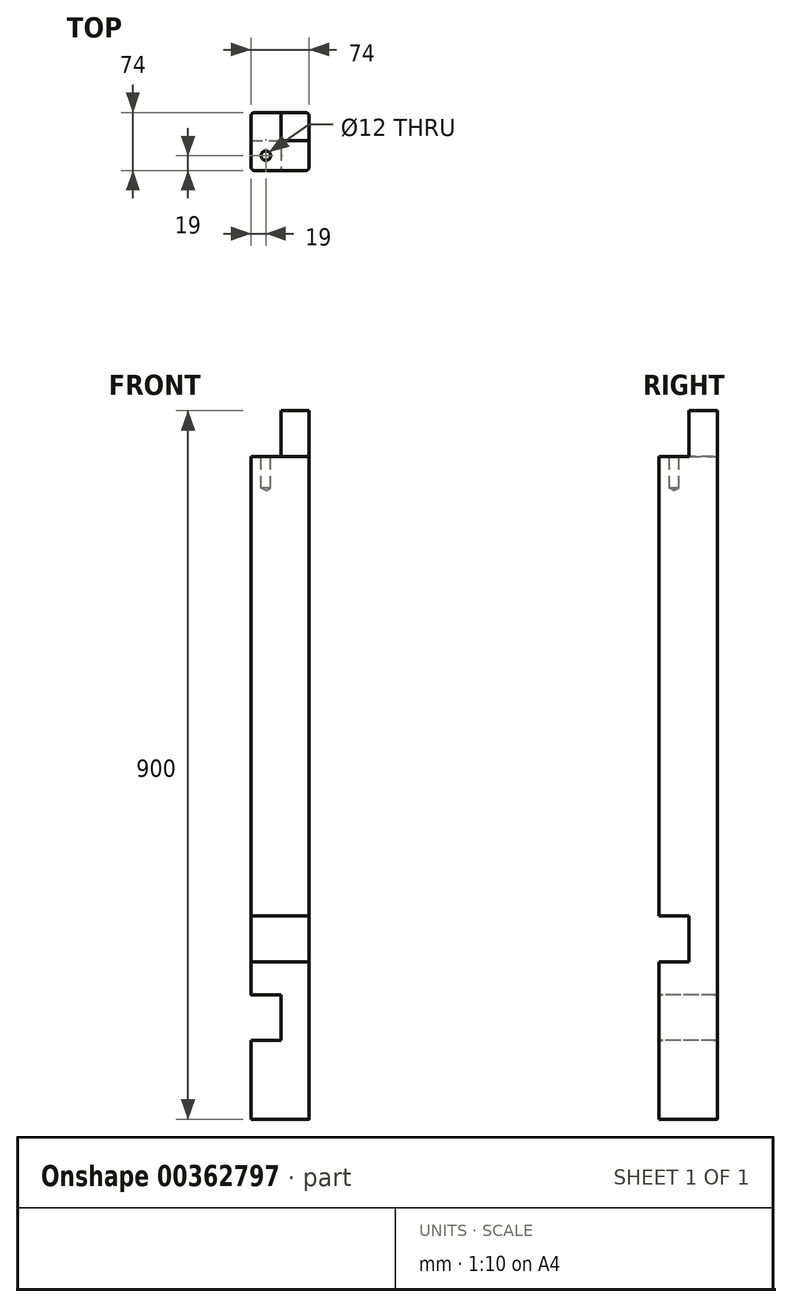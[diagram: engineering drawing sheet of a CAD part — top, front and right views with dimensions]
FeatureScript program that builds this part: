
annotation { "Feature Type Name" : "Feature", "Feature Type Description" : "" }
export const myFeature = defineFeature(function(context is Context, id is Id, definition is map)
    precondition{}
    {
        {
            var Q0;
            Q0=qCreatedBy(makeId("Top.planeOp"),FACE);
            var sketch = newSketch(context, id + "F0", { "sketchPlane" : qUnion([Q0])});
            skLineSegment(sketch, "E0.bottom", {"start": v(37, 37) * mm, "end": v(-37, 37) * mm});
            skLineSegment(sketch, "E0.top", {"start": v(37, -37) * mm, "end": v(-37, -37) * mm});
            skLineSegment(sketch, "E0.left", {"start": v(37, 37) * mm, "end": v(37, -37) * mm});
            skLineSegment(sketch, "E0.right", {"start": v(-37, 37) * mm, "end": v(-37, -37) * mm});
            skPoint(sketch, "E0.middle", {"position": v(0, 0) * mm});
            skSolve(sketch);
        }
        {
            var Q0;
            Q0=makeQuery(id+"F0.imprint","IMPRINT",FACE,{"disambiguationData":[TD([[makeQuery(id+"F0.imprint","IMPRINT",EDGE,{"derivedFrom":sQuery(id+"F0.wireOp",EDGE,"E0.bottom")}),1.0]])]});
            extrude(context, id + "F1", {"entities" : qUnion([Q0]), "oppositeDirection" : true, "depth" : 900 * mm});
        }
        {
            var Q0;
            Q0=makeQuery(id+"F1.opExtrude","SWEPT_FACE",FACE,{"disambiguationData":[OSD([sQuery(id+"F0.wireOp",EDGE,"E0.top")])]});
            var sketch = newSketch(context, id + "F2", { "sketchPlane" : qUnion([Q0])});
            skLineSegment(sketch, "E1", {"start": v(-37, -58) * mm, "end": v(37, -58) * mm});
            skSolve(sketch);
        }
        {
            var Q0;
            Q0=makeQuery(id+"F1.opExtrude","SWEPT_FACE",FACE,{"disambiguationData":[OSD([sQuery(id+"F0.wireOp",EDGE,"E0.right")])]});
            var sketch = newSketch(context, id + "F3", { "sketchPlane" : qUnion([Q0])});
            skLineSegment(sketch, "E2", {"start": v(37, -58) * mm, "end": v(-37, -58) * mm});
            skSolve(sketch);
        }
        {
            var Q0;
            {var subQ0=sQuery(id+"F2.wireOp",EDGE,"E1");Q0=makeQuery(id+"F2.imprint","IMPRINT",FACE,{"disambiguationData":[TD([[makeQuery(id+"F2.imprint","IMPRINT",EDGE,{"derivedFrom":subQ0}),1.0]])]});}
            extrude(context, id + "F4", {"entities" : qUnion([Q0]), "operationType" : NewBodyOperationType.REMOVE, "oppositeDirection" : true, "depth" : 38 * mm});
        }
        {
            var Q0;
            {var subQ0=sQuery(id+"F3.wireOp",EDGE,"E2");Q0=makeQuery(id+"F3.imprint","IMPRINT",FACE,{"disambiguationData":[TD([[makeQuery(id+"F3.imprint","IMPRINT",EDGE,{"derivedFrom":subQ0}),-1.0]])]});}
            extrude(context, id + "F5", {"entities" : qUnion([Q0]), "operationType" : NewBodyOperationType.REMOVE, "oppositeDirection" : true, "depth" : 38 * mm});
        }
        {
            var Q0;
            Q0=makeQuery(id+"F5.boolean.opBoolean","MERGE",FACE,{"derivedFrom":[makeQuery(id+"F4.boolean.opBoolean","COPY",FACE,{"derivedFrom":makeQuery(id+"F4.opExtrude","SWEPT_FACE",FACE,{"disambiguationData":[OSD([sQuery(id+"F2.wireOp",EDGE,"E1")])]})}),makeQuery(id+"F5.opExtrude","SWEPT_FACE",FACE,{"disambiguationData":[OSD([sQuery(id+"F3.wireOp",EDGE,"E2")])]})]});
            var sketch = newSketch(context, id + "F6", { "sketchPlane" : qUnion([Q0])});
            skPoint(sketch, "E3", {"position": v(-18, -18) * mm});
            skSolve(sketch);
        }
        {
            var Q0;
            Q0=sQuery(id+"F6.wireOp",VERTEX,"E3");
            var Q1;
            Q1=makeQuery(id+"F1.opExtrude","SWEPT_BODY",BODY,{"disambiguationData":[OSD([sQuery(id+"F0.wireOp",EDGE,"E0.bottom"),sQuery(id+"F0.wireOp",EDGE,"E0.top"),sQuery(id+"F0.wireOp",EDGE,"E0.left"),sQuery(id+"F0.wireOp",EDGE,"E0.right")])]});
            hole(context, id + "F7", {"style" : HoleStyle.SIMPLE, "endStyle" : HoleEndStyle.BLIND, "holeDiameter" : 12 * mm, "holeDepth" : 40 * mm, "isTappedThrough" : true, "tappedDepth" : 12 * mm, "tapClearance" : 3, "locations" : qUnion([Q0]), "scope" : qUnion([Q1])});
        }
        {
            var Q0;
            Q0=makeQuery(id+"F1.opExtrude","SWEPT_FACE",FACE,{"disambiguationData":[OSD([sQuery(id+"F0.wireOp",EDGE,"E0.right")])]});
            var sketch = newSketch(context, id + "F8", { "sketchPlane" : qUnion([Q0])});
            skLineSegment(sketch, "E4", {"start": v(-37, -742) * mm, "end": v(37, -742) * mm});
            skLineSegment(sketch, "E5", {"start": v(-37, -800) * mm, "end": v(37, -800) * mm});
            skSolve(sketch);
        }
        {
            var Q0;
            {var subQ0=sQuery(id+"F8.wireOp",EDGE,"E4");Q0=makeQuery(id+"F8.imprint","IMPRINT",FACE,{"disambiguationData":[TD([[makeQuery(id+"F8.imprint","IMPRINT",EDGE,{"derivedFrom":subQ0}),-1.0]])]});}
            extrude(context, id + "F9", {"entities" : qUnion([Q0]), "operationType" : NewBodyOperationType.REMOVE, "oppositeDirection" : true, "depth" : 38 * mm});
        }
        {
            var Q0;
            Q0=makeQuery(id+"F1.opExtrude","SWEPT_FACE",FACE,{"disambiguationData":[OSD([sQuery(id+"F0.wireOp",EDGE,"E0.top")])]});
            var sketch = newSketch(context, id + "F10", { "sketchPlane" : qUnion([Q0])});
            skLineSegment(sketch, "E6", {"start": v(-37, -700) * mm, "end": v(37, -700) * mm});
            skLineSegment(sketch, "E7", {"start": v(-37, -642) * mm, "end": v(37, -642) * mm});
            skSolve(sketch);
        }
        {
            var Q0;
            {var subQ0=sQuery(id+"F10.wireOp",EDGE,"E6");Q0=makeQuery(id+"F10.imprint","IMPRINT",FACE,{"disambiguationData":[TD([[makeQuery(id+"F10.imprint","IMPRINT",EDGE,{"derivedFrom":subQ0}),1.0]])]});}
            extrude(context, id + "F11", {"entities" : qUnion([Q0]), "operationType" : NewBodyOperationType.REMOVE, "oppositeDirection" : true, "depth" : 38 * mm});
        }
        {
            var Q0;
            Q0=makeQuery(id+"F1.opExtrude","SWEPT_EDGE",EDGE,{"disambiguationData":[OSD([sQuery(id+"F0.wireOp",EDGE,"E0.top"),sQuery(id+"F0.wireOp",EDGE,"E0.right")])]});
            var Q1;
            Q1=makeQuery(id+"F1.opExtrude","SWEPT_EDGE",EDGE,{"disambiguationData":[OSD([sQuery(id+"F0.wireOp",EDGE,"E0.bottom"),sQuery(id+"F0.wireOp",EDGE,"E0.right")])]});
            var Q2;
            Q2=makeQuery(id+"F1.opExtrude","SWEPT_EDGE",EDGE,{"disambiguationData":[OSD([sQuery(id+"F0.wireOp",EDGE,"E0.top"),sQuery(id+"F0.wireOp",EDGE,"E0.left")])]});
            var Q3;
            Q3=makeQuery(id+"F1.opExtrude","SWEPT_EDGE",EDGE,{"disambiguationData":[OSD([sQuery(id+"F0.wireOp",EDGE,"E0.bottom"),sQuery(id+"F0.wireOp",EDGE,"E0.left")])]});
            fillet(context, id + "F12", {"entities" : qUnion([Q0, Q1, Q2, Q3]), "radius" : 5 * mm, "tangentPropagation" : true, "allowEdgeOverflow" : false});
        }
    });
